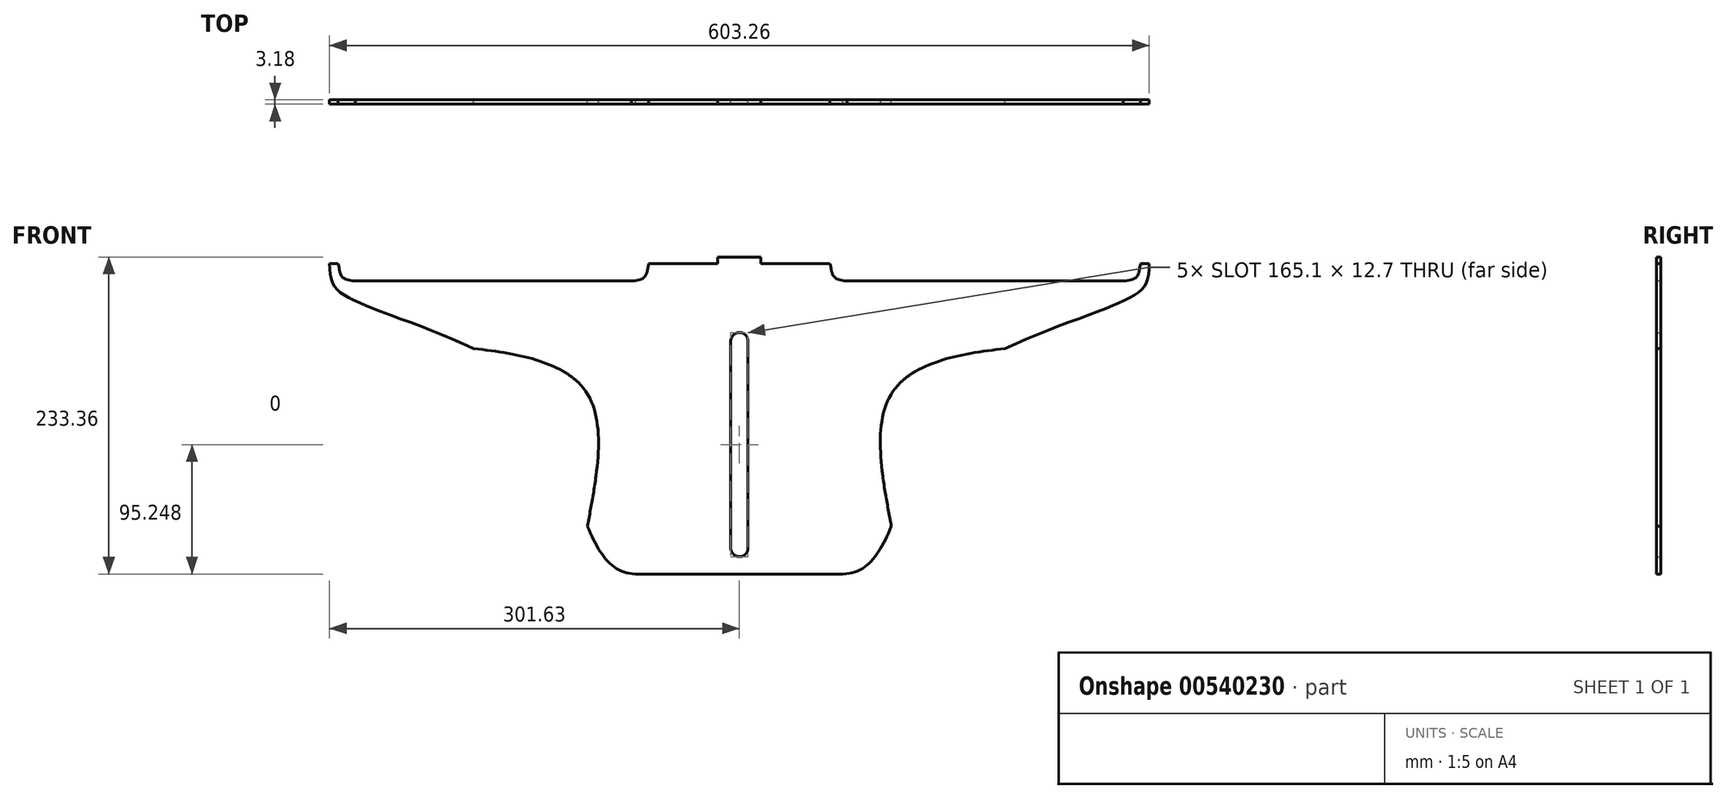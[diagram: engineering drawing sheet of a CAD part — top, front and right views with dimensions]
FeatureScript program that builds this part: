
annotation { "Feature Type Name" : "Feature", "Feature Type Description" : "" }
export const myFeature = defineFeature(function(context is Context, id is Id, definition is map)
    precondition{}
    {
        {
            var Q0;
            Q0=qCreatedBy(makeId("Front.planeOp"),FACE);
            var sketch = newSketch(context, id + "F0", { "sketchPlane" : qUnion([Q0])});
            skLineSegment(sketch, "E0", {"start": v(-320.68, -4.76) * mm, "end": v(-295.28, -4.76) * mm});
            skLineSegment(sketch, "E1", {"start": v(-15.88, -4.76) * mm, "end": v(-15.88, 0) * mm});
            skLineSegment(sketch, "E2", {"start": v(-15.88, 0) * mm, "end": v(15.88, 0) * mm});
            skLineSegment(sketch, "E3", {"start": v(15.87, 0) * mm, "end": v(15.87, -4.76) * mm});
            skLineSegment(sketch, "E4", {"start": v(15.87, -4.76) * mm, "end": v(66.67, -4.76) * mm});
            skFitSpline(sketch, "E5", {"points": [v(-320.68, -4.76) * mm, v(-289.75, -50.06) * mm, v(-142.46, -131.38) * mm, v(-76.2, -233.36) * mm], "startDerivative": vector(3.08, -322.5) * mm, "endDerivative": vector(316.98, -6.18) * mm});
            skLineSegment(sketch, "E6", {"start": v(0, 0) * mm, "end": v(0, -233.36) * mm, "construction": true});
            skPoint(sketch, "E7", {"position": v(0, 0) * mm});
            skLineSegment(sketch, "E8", {"start": v(0, -233.36) * mm, "end": v(-76.2, -233.36) * mm});
            skLineSegment(sketch, "E9", {"start": v(0, -233.36) * mm, "end": v(76.2, -233.36) * mm});
            skFitSpline(sketch, "E10.MirrorCS", {"points": [v(320.68, -4.76) * mm, v(289.75, -50.06) * mm, v(142.46, -131.38) * mm, v(76.2, -233.36) * mm], "startDerivative": vector(-3.08, -322.5) * mm, "endDerivative": vector(-316.98, -6.18) * mm});
            skLineSegment(sketch, "E11", {"start": v(15.87, -4.76) * mm, "end": v(-15.87, -4.76) * mm, "construction": true});
            skFitSpline(sketch, "E12.0", {"points": [v(-320.68, -4.76) * mm, v(-320.43, -30.11) * mm, v(-295.08, -57.7) * mm, v(-112.97, -99) * mm, v(-113.3, -232.64) * mm, v(-76.2, -233.36) * mm]});
            skLineSegment(sketch, "E12.1", {"start": v(-44.45, -204.66) * mm, "end": v(-87.62, -204.66) * mm});
            skLineSegment(sketch, "E12.3", {"start": v(72.92, -33.46) * mm, "end": v(280.22, -33.46) * mm});
            skFitSpline(sketch, "E12.4", {"points": [v(320.68, -4.76) * mm, v(320.43, -30.11) * mm, v(295.08, -57.7) * mm, v(112.97, -99) * mm, v(113.3, -232.64) * mm, v(76.2, -233.36) * mm]});
            skLineSegment(sketch, "E12.5", {"start": v(-280.22, -33.46) * mm, "end": v(-72.92, -33.46) * mm});
            skLineSegment(sketch, "E12.6", {"start": v(44.45, -204.66) * mm, "end": v(87.62, -204.66) * mm});
            skFitSpline(sketch, "E13", {"points": [v(-44.45, -33.46) * mm, v(-19.05, -53.41) * mm, v(-19.05, -95.34) * mm, v(-19.05, -131.83) * mm, v(-19.05, -164.67) * mm, v(-19.05, -188.89) * mm, v(-44.45, -204.66) * mm], "startDerivative": vector(397.66, 0) * mm, "endDerivative": vector(-432.74, 0) * mm});
            skFitSpline(sketch, "E14.MirrorCS", {"points": [v(44.45, -33.46) * mm, v(19.05, -53.41) * mm, v(19.05, -95.34) * mm, v(19.05, -131.83) * mm, v(19.05, -164.67) * mm, v(19.05, -188.89) * mm, v(44.45, -204.66) * mm], "startDerivative": vector(-397.66, 0) * mm, "endDerivative": vector(432.74, 0) * mm});
            skLineSegment(sketch, "E15", {"start": v(-6.35, -61.91) * mm, "end": v(-6.35, -214.31) * mm});
            skLineSegment(sketch, "E16", {"start": v(6.35, -61.91) * mm, "end": v(6.35, -214.31) * mm});
            skLineSegment(sketch, "E17", {"start": v(6.35, -214.31) * mm, "end": v(9.09, -214.31) * mm});
            skArc(sketch, "E18", {"start": v(6.35, -61.91) * mm, "mid": v(0, -55.56) * mm, "end": v(-6.35, -61.91) * mm});
            skArc(sketch, "E19", {"start": v(-6.35, -214.31) * mm, "mid": v(0, -220.66) * mm, "end": v(6.35, -214.31) * mm});
            skLineSegment(sketch, "E20", {"start": v(6.35, -138.11) * mm, "end": v(-6.35, -138.11) * mm, "construction": true});
            skLineSegment(sketch, "E21", {"start": v(-15.93, -220.66) * mm, "end": v(15.93, -220.66) * mm, "construction": true});
            skPoint(sketch, "E22", {"position": v(0, -220.66) * mm});
            skLineSegment(sketch, "E23", {"start": v(-282.58, -17.46) * mm, "end": v(-68.43, -17.46) * mm});
            skFitSpline(sketch, "E24", {"points": [v(-282.58, -17.46) * mm, v(-294, -11.11) * mm, v(-295.28, -4.76) * mm], "startDerivative": vector(-45.38, -1.82) * mm, "endDerivative": vector(-6.58, 25.27) * mm});
            skPoint(sketch, "E25", {"position": v(-68.43, -17.46) * mm});
            skLineSegment(sketch, "E26.MirrorCS", {"start": v(-79.37, -17.46) * mm, "end": v(-282.58, -17.46) * mm});
            skPoint(sketch, "E27", {"position": v(-168.28, -4.76) * mm});
            skFitSpline(sketch, "E28.MirrorCS", {"points": [v(-79.38, -17.46) * mm, v(-67.95, -11.11) * mm, v(-66.68, -4.76) * mm], "startDerivative": vector(45.38, -1.82) * mm, "endDerivative": vector(6.58, 25.27) * mm});
            skFitSpline(sketch, "E29", {"points": [v(79.38, -17.46) * mm, v(67.95, -11.11) * mm, v(66.68, -4.76) * mm], "startDerivative": vector(-45.38, -1.82) * mm, "endDerivative": vector(-6.58, 25.27) * mm});
            skLineSegment(sketch, "E30.MirrorCS", {"start": v(282.58, -17.46) * mm, "end": v(79.37, -17.46) * mm});
            skFitSpline(sketch, "E31.MirrorCS", {"points": [v(282.58, -17.46) * mm, v(294, -11.11) * mm, v(295.28, -4.76) * mm], "startDerivative": vector(45.38, -1.82) * mm, "endDerivative": vector(6.58, 25.27) * mm});
            skFitSpline(sketch, "E32.MirrorCS", {"points": [v(79.38, -17.46) * mm, v(67.95, -11.11) * mm, v(66.67, -4.76) * mm], "startDerivative": vector(-45.38, -1.82) * mm, "endDerivative": vector(-6.58, 25.27) * mm});
            skLineSegment(sketch, "E33.MirrorCS", {"start": v(79.37, -17.46) * mm, "end": v(282.57, -17.46) * mm});
            skFitSpline(sketch, "E34.MirrorCS", {"points": [v(282.58, -17.46) * mm, v(294, -11.11) * mm, v(295.27, -4.76) * mm], "startDerivative": vector(45.38, -1.82) * mm, "endDerivative": vector(6.58, 25.27) * mm});
            skLineSegment(sketch, "E35.trimOffspring", {"start": v(295.27, -4.76) * mm, "end": v(320.68, -4.76) * mm});
            skLineSegment(sketch, "E36.trimOffspring", {"start": v(-180.97, -4.76) * mm, "end": v(-168.28, -4.76) * mm});
            skFitSpline(sketch, "E37.0", {"points": [v(301.63, -4.58) * mm, v(301.6, -7.33) * mm, v(301.37, -10.9) * mm, v(300.77, -14.56) * mm, v(300.23, -16.8) * mm, v(299.61, -18.63) * mm, v(298.95, -20.1) * mm, v(298.22, -21.37) * mm, v(297.38, -22.54) * mm, v(296.35, -23.72) * mm, v(295.03, -24.96) * mm, v(293.35, -26.3) * mm, v(291.25, -27.75) * mm, v(288.69, -29.28) * mm, v(285.67, -30.9) * mm, v(282.18, -32.6) * mm, v(278.23, -34.36) * mm, v(273.88, -36.2) * mm, v(267.58, -38.71) * mm, v(258.9, -42.01) * mm, v(247.46, -46.24) * mm, v(235.23, -50.8) * mm, v(222.43, -55.77) * mm, v(209.29, -61.23) * mm, v(196, -67.3) * mm, v(182.76, -74.05) * mm, v(169.76, -81.62) * mm, v(159.31, -88.72) * mm, v(151.29, -94.95) * mm, v(145.47, -99.91) * mm, v(139.88, -105.19) * mm, v(135.45, -109.86) * mm, v(132.05, -113.77) * mm, v(130, -116.3) * mm, v(128.4, -118.35) * mm, v(127.22, -119.92) * mm, v(126.07, -121.51) * mm, v(124.58, -123.64) * mm, v(122.79, -126.32) * mm, v(120.08, -130.66) * mm, v(116.95, -136.13) * mm, v(113.57, -142.73) * mm, v(109.48, -151.52) * mm, v(105.02, -162.35) * mm, v(100.38, -174.75) * mm, v(96.14, -186.16) * mm, v(92.75, -194.49) * mm, v(90.07, -200.2) * mm, v(88.1, -203.92) * mm, v(86.18, -207.05) * mm, v(84.36, -209.53) * mm, v(82.7, -211.35) * mm, v(81.28, -212.58) * mm, v(80.09, -213.35) * mm, v(79, -213.83) * mm, v(77.72, -214.18) * mm, v(76.54, -214.3) * mm, v(75.83, -214.32) * mm]});
            skFitSpline(sketch, "E38.trimOffspring", {"points": [v(301.63, -4.58) * mm, v(301.6, -7.33) * mm, v(301.37, -10.9) * mm, v(300.77, -14.56) * mm, v(300.23, -16.8) * mm, v(299.61, -18.63) * mm, v(298.95, -20.1) * mm, v(298.22, -21.37) * mm, v(297.38, -22.54) * mm, v(296.35, -23.72) * mm, v(295.03, -24.96) * mm, v(293.35, -26.3) * mm, v(291.25, -27.75) * mm, v(288.69, -29.28) * mm, v(285.67, -30.9) * mm, v(282.18, -32.6) * mm, v(278.23, -34.36) * mm, v(273.88, -36.2) * mm, v(267.58, -38.71) * mm, v(258.9, -42.01) * mm, v(247.46, -46.24) * mm, v(235.23, -50.8) * mm, v(222.43, -55.77) * mm, v(209.29, -61.23) * mm, v(196, -67.3) * mm, v(182.76, -74.05) * mm, v(169.76, -81.62) * mm, v(159.31, -88.72) * mm, v(151.29, -94.95) * mm, v(145.47, -99.91) * mm, v(139.88, -105.19) * mm, v(135.45, -109.86) * mm, v(132.05, -113.77) * mm, v(130, -116.3) * mm, v(128.4, -118.35) * mm, v(127.22, -119.92) * mm, v(126.07, -121.51) * mm, v(124.58, -123.64) * mm, v(122.79, -126.32) * mm, v(120.08, -130.66) * mm, v(116.95, -136.13) * mm, v(113.57, -142.73) * mm, v(109.48, -151.52) * mm, v(105.02, -162.35) * mm, v(100.38, -174.75) * mm, v(96.14, -186.16) * mm, v(92.75, -194.49) * mm, v(90.07, -200.2) * mm, v(88.1, -203.92) * mm, v(86.18, -207.05) * mm, v(84.36, -209.53) * mm, v(82.7, -211.35) * mm, v(81.28, -212.58) * mm, v(80.09, -213.35) * mm, v(79, -213.83) * mm, v(77.72, -214.18) * mm, v(76.54, -214.3) * mm, v(75.83, -214.32) * mm]});
            skFitSpline(sketch, "E39.0", {"points": [v(-301.63, -4.58) * mm, v(-301.6, -7.33) * mm, v(-301.37, -10.9) * mm, v(-300.77, -14.56) * mm, v(-300.23, -16.8) * mm, v(-299.61, -18.63) * mm, v(-298.95, -20.1) * mm, v(-298.22, -21.37) * mm, v(-297.38, -22.54) * mm, v(-296.35, -23.72) * mm, v(-295.03, -24.96) * mm, v(-293.35, -26.3) * mm, v(-291.25, -27.75) * mm, v(-288.69, -29.28) * mm, v(-285.67, -30.9) * mm, v(-282.18, -32.6) * mm, v(-278.23, -34.36) * mm, v(-273.88, -36.2) * mm, v(-267.58, -38.71) * mm, v(-258.9, -42.01) * mm, v(-247.46, -46.24) * mm, v(-235.23, -50.8) * mm, v(-222.43, -55.77) * mm, v(-209.29, -61.23) * mm, v(-196, -67.3) * mm, v(-182.76, -74.05) * mm, v(-169.76, -81.62) * mm, v(-159.31, -88.72) * mm, v(-151.29, -94.95) * mm, v(-145.47, -99.91) * mm, v(-139.88, -105.19) * mm, v(-135.45, -109.86) * mm, v(-132.05, -113.77) * mm, v(-130, -116.3) * mm, v(-128.4, -118.35) * mm, v(-127.22, -119.92) * mm, v(-126.07, -121.51) * mm, v(-124.58, -123.64) * mm, v(-122.79, -126.32) * mm, v(-120.08, -130.66) * mm, v(-116.95, -136.13) * mm, v(-113.57, -142.73) * mm, v(-109.48, -151.52) * mm, v(-105.02, -162.35) * mm, v(-100.38, -174.75) * mm, v(-96.14, -186.16) * mm, v(-92.75, -194.49) * mm, v(-90.07, -200.2) * mm, v(-88.1, -203.92) * mm, v(-86.18, -207.05) * mm, v(-84.36, -209.53) * mm, v(-82.7, -211.35) * mm, v(-81.28, -212.58) * mm, v(-80.09, -213.35) * mm, v(-79, -213.83) * mm, v(-77.72, -214.18) * mm, v(-76.54, -214.3) * mm, v(-75.83, -214.32) * mm]});
            skFitSpline(sketch, "E40.trimOffspring", {"points": [v(-301.63, -4.58) * mm, v(-301.6, -7.33) * mm, v(-301.37, -10.9) * mm, v(-300.77, -14.56) * mm, v(-300.23, -16.8) * mm, v(-299.61, -18.63) * mm, v(-298.95, -20.1) * mm, v(-298.22, -21.37) * mm, v(-297.38, -22.54) * mm, v(-296.35, -23.72) * mm, v(-295.03, -24.96) * mm, v(-293.35, -26.3) * mm, v(-291.25, -27.75) * mm, v(-288.69, -29.28) * mm, v(-285.67, -30.9) * mm, v(-282.18, -32.6) * mm, v(-278.23, -34.36) * mm, v(-273.88, -36.2) * mm, v(-267.58, -38.71) * mm, v(-258.9, -42.01) * mm, v(-247.46, -46.24) * mm, v(-235.23, -50.8) * mm, v(-222.43, -55.77) * mm, v(-209.29, -61.23) * mm, v(-196, -67.3) * mm, v(-182.76, -74.05) * mm, v(-169.76, -81.62) * mm, v(-159.31, -88.72) * mm, v(-151.29, -94.95) * mm, v(-145.47, -99.91) * mm, v(-139.88, -105.19) * mm, v(-135.45, -109.86) * mm, v(-132.05, -113.77) * mm, v(-130, -116.3) * mm, v(-128.4, -118.35) * mm, v(-127.22, -119.92) * mm, v(-126.07, -121.51) * mm, v(-124.58, -123.64) * mm, v(-122.79, -126.32) * mm, v(-120.08, -130.66) * mm, v(-116.95, -136.13) * mm, v(-113.57, -142.73) * mm, v(-109.48, -151.52) * mm, v(-105.02, -162.35) * mm, v(-100.38, -174.75) * mm, v(-96.14, -186.16) * mm, v(-92.75, -194.49) * mm, v(-90.07, -200.2) * mm, v(-88.1, -203.92) * mm, v(-86.18, -207.05) * mm, v(-84.36, -209.53) * mm, v(-82.7, -211.35) * mm, v(-81.28, -212.58) * mm, v(-80.09, -213.35) * mm, v(-79, -213.83) * mm, v(-77.72, -214.18) * mm, v(-76.54, -214.3) * mm, v(-75.83, -214.32) * mm]});
            skLineSegment(sketch, "E41.trimOffspring", {"start": v(77.32, -17.46) * mm, "end": v(145.72, -17.46) * mm});
            skLineSegment(sketch, "E42.trimOffspring", {"start": v(-66.68, -4.76) * mm, "end": v(-15.87, -4.76) * mm});
            skPoint(sketch, "E43", {"position": v(0, -4.76) * mm});
            skFitSpline(sketch, "E44", {"points": [v(-158.28, -89.62) * mm, v(-124.96, -81.72) * mm, v(-80.36, -54.99) * mm, v(-72.05, -40.47) * mm, v(-72.92, -33.46) * mm], "startDerivative": vector(96.89, -21.66) * mm, "endDerivative": vector(-12.62, 48.23) * mm});
            skFitSpline(sketch, "E45", {"points": [v(-131.33, -114.67) * mm, v(-126.63, -100.34) * mm, v(-95.43, -77.9) * mm, v(-43.57, -59.54) * mm, v(-22.8, -65.1) * mm, v(-18.53, -73.9) * mm], "startDerivative": vector(27.16, 115.79) * mm, "endDerivative": vector(19.4, -71.27) * mm});
            skFitSpline(sketch, "E46.trimOffspring", {"points": [v(-301.63, -4.58) * mm, v(-301.6, -7.33) * mm, v(-301.37, -10.9) * mm, v(-300.77, -14.56) * mm, v(-300.23, -16.8) * mm, v(-299.61, -18.63) * mm, v(-298.95, -20.1) * mm, v(-298.22, -21.37) * mm, v(-297.38, -22.54) * mm, v(-296.35, -23.72) * mm, v(-295.03, -24.96) * mm, v(-293.35, -26.3) * mm, v(-291.25, -27.75) * mm, v(-288.69, -29.28) * mm, v(-285.67, -30.9) * mm, v(-282.18, -32.6) * mm, v(-278.23, -34.36) * mm, v(-273.88, -36.2) * mm, v(-267.58, -38.71) * mm, v(-258.9, -42.01) * mm, v(-247.46, -46.24) * mm, v(-235.23, -50.8) * mm, v(-222.43, -55.77) * mm, v(-209.29, -61.23) * mm, v(-196, -67.3) * mm, v(-182.76, -74.05) * mm, v(-169.76, -81.62) * mm, v(-159.31, -88.72) * mm, v(-151.29, -94.95) * mm, v(-145.47, -99.91) * mm, v(-139.88, -105.19) * mm, v(-135.45, -109.86) * mm, v(-132.05, -113.77) * mm, v(-130, -116.3) * mm, v(-128.4, -118.35) * mm, v(-127.22, -119.92) * mm, v(-126.07, -121.51) * mm, v(-124.58, -123.64) * mm, v(-122.79, -126.32) * mm, v(-120.08, -130.66) * mm, v(-116.95, -136.13) * mm, v(-113.57, -142.73) * mm, v(-109.48, -151.52) * mm, v(-105.02, -162.35) * mm, v(-100.38, -174.75) * mm, v(-96.14, -186.16) * mm, v(-92.75, -194.49) * mm, v(-90.07, -200.2) * mm, v(-88.1, -203.92) * mm, v(-86.18, -207.05) * mm, v(-84.36, -209.53) * mm, v(-82.7, -211.35) * mm, v(-81.28, -212.58) * mm, v(-80.09, -213.35) * mm, v(-79, -213.83) * mm, v(-77.72, -214.18) * mm, v(-76.54, -214.3) * mm, v(-75.83, -214.32) * mm]});
            skFitSpline(sketch, "E47.MirrorCS", {"points": [v(158.28, -89.62) * mm, v(124.96, -81.72) * mm, v(80.36, -54.99) * mm, v(72.05, -40.47) * mm, v(72.92, -33.46) * mm], "startDerivative": vector(-96.89, -21.66) * mm, "endDerivative": vector(12.62, 48.23) * mm});
            skFitSpline(sketch, "E48.MirrorCS", {"points": [v(131.33, -114.67) * mm, v(126.63, -100.34) * mm, v(95.43, -77.9) * mm, v(43.57, -59.54) * mm, v(22.8, -65.1) * mm, v(18.53, -73.9) * mm], "startDerivative": vector(-27.16, 115.79) * mm, "endDerivative": vector(-19.4, -71.27) * mm});
            skFitSpline(sketch, "E49.trimOffspring", {"points": [v(301.63, -4.58) * mm, v(301.6, -7.33) * mm, v(301.37, -10.9) * mm, v(300.77, -14.56) * mm, v(300.23, -16.8) * mm, v(299.61, -18.63) * mm, v(298.95, -20.1) * mm, v(298.22, -21.37) * mm, v(297.38, -22.54) * mm, v(296.35, -23.72) * mm, v(295.03, -24.96) * mm, v(293.35, -26.3) * mm, v(291.25, -27.75) * mm, v(288.69, -29.28) * mm, v(285.67, -30.9) * mm, v(282.18, -32.6) * mm, v(278.23, -34.36) * mm, v(273.88, -36.2) * mm, v(267.58, -38.71) * mm, v(258.9, -42.01) * mm, v(247.46, -46.24) * mm, v(235.23, -50.8) * mm, v(222.43, -55.77) * mm, v(209.29, -61.23) * mm, v(196, -67.3) * mm, v(182.76, -74.05) * mm, v(169.76, -81.62) * mm, v(159.31, -88.72) * mm, v(151.29, -94.95) * mm, v(145.47, -99.91) * mm, v(139.88, -105.19) * mm, v(135.45, -109.86) * mm, v(132.05, -113.77) * mm, v(130, -116.3) * mm, v(128.4, -118.35) * mm, v(127.22, -119.92) * mm, v(126.07, -121.51) * mm, v(124.58, -123.64) * mm, v(122.79, -126.32) * mm, v(120.08, -130.66) * mm, v(116.95, -136.13) * mm, v(113.57, -142.73) * mm, v(109.48, -151.52) * mm, v(105.02, -162.35) * mm, v(100.38, -174.75) * mm, v(96.14, -186.16) * mm, v(92.75, -194.49) * mm, v(90.07, -200.2) * mm, v(88.1, -203.92) * mm, v(86.18, -207.05) * mm, v(84.36, -209.53) * mm, v(82.7, -211.35) * mm, v(81.28, -212.58) * mm, v(80.09, -213.35) * mm, v(79, -213.83) * mm, v(77.72, -214.18) * mm, v(76.54, -214.3) * mm, v(75.83, -214.32) * mm]});
            skSolve(sketch);
        }
        {
            var Q0;
            {var subQ6=sQuery(id+"F0.wireOp",EDGE,"E1");Q0=makeQuery(id+"F0.imprint","IMPRINT",FACE,{"disambiguationData":[TD([[makeQuery(id+"F0.imprint","IMPRINT",EDGE,{"derivedFrom":subQ6}),-1.0]])]});}
            extrude(context, id + "F1", {"entities" : qUnion([Q0]), "depth" : 3.17 * mm, "offsetDistance" : 25.4 * mm});
        }
    });
